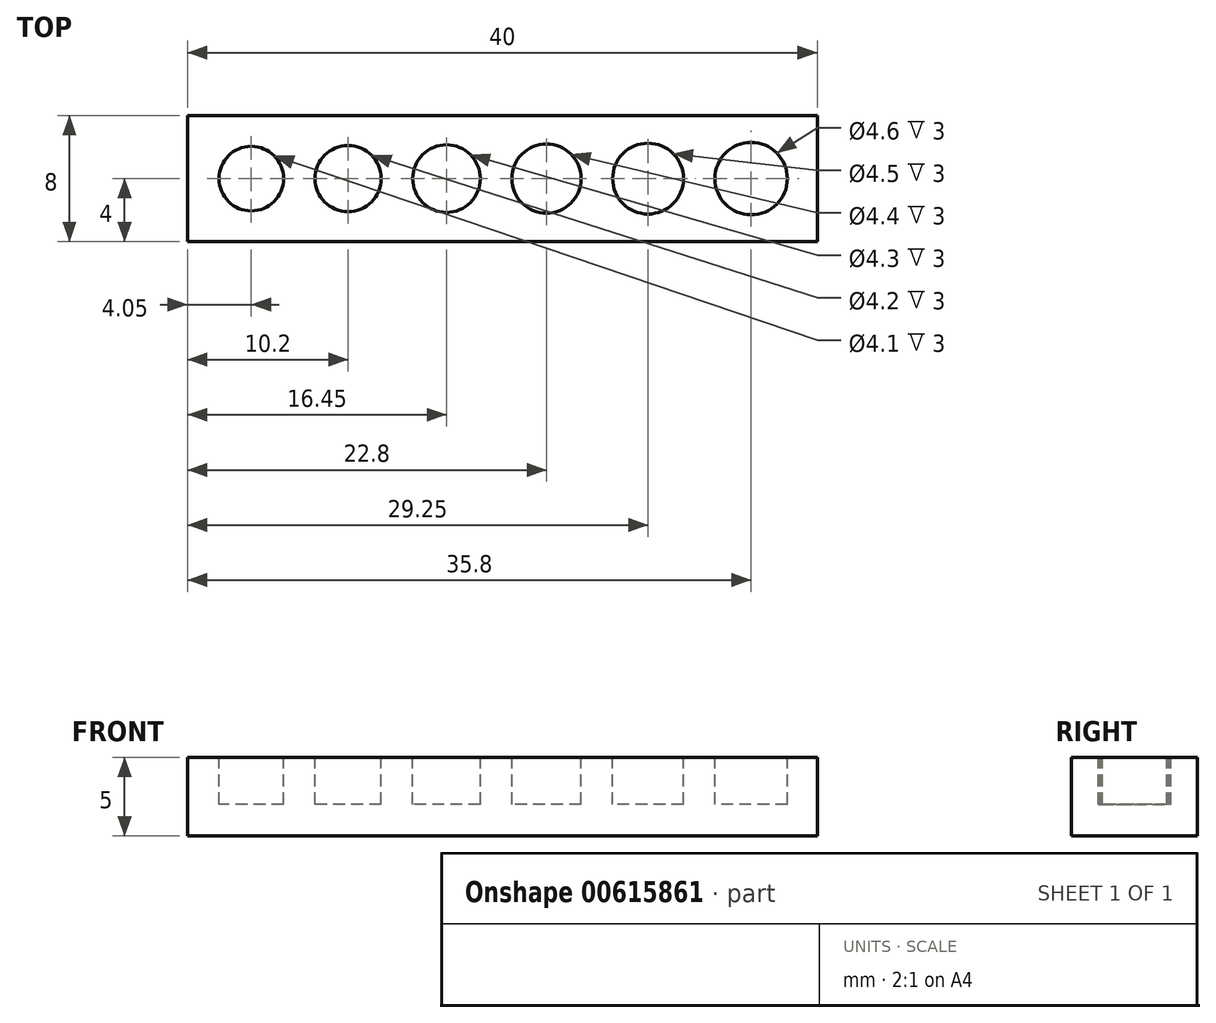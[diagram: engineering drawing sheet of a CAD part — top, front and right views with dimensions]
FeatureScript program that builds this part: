
annotation { "Feature Type Name" : "Feature", "Feature Type Description" : "" }
export const myFeature = defineFeature(function(context is Context, id is Id, definition is map)
    precondition{}
    {
        {
            var Q0;
            Q0=qCreatedBy(makeId("Top.planeOp"),FACE);
            var sketch = newSketch(context, id + "F0", { "sketchPlane" : qUnion([Q0])});
            skLineSegment(sketch, "E0.bottom", {"start": v(0, 0) * mm, "end": v(40, 0) * mm});
            skLineSegment(sketch, "E0.top", {"start": v(0, -8) * mm, "end": v(40, -8) * mm});
            skLineSegment(sketch, "E0.left", {"start": v(0, 0) * mm, "end": v(0, -8) * mm});
            skLineSegment(sketch, "E0.right", {"start": v(40, 0) * mm, "end": v(40, -8) * mm});
            skSolve(sketch);
        }
        {
            var Q0;
            Q0 = qSketchRegion(id + "F0", true);
            extrude(context, id + "F1", {"entities" : qUnion([Q0]), "depth" : 5 * mm, "offsetDistance" : 25 * mm});
        }
        {
            var Q0;
            Q0=makeQuery(id+"F1.opExtrude","CAP_FACE",FACE,{"disambiguationData":[OSD([sQuery(id+"F0.wireOp",EDGE,"E0.bottom"),sQuery(id+"F0.wireOp",EDGE,"E0.top"),sQuery(id+"F0.wireOp",EDGE,"E0.left"),sQuery(id+"F0.wireOp",EDGE,"E0.right")])],"isStart":false});
            var sketch = newSketch(context, id + "F2", { "sketchPlane" : qUnion([Q0])});
            skLineSegment(sketch, "E1", {"start": v(0, -4) * mm, "end": v(40, -4) * mm, "construction": true});
            skCircle(sketch, "E2", {"center": v(4.05, -4) * mm, "radius": 2.05 * mm});
            skCircle(sketch, "E3", {"center": v(10.2, -4) * mm, "radius": 2.1 * mm});
            skCircle(sketch, "E4", {"center": v(16.45, -4) * mm, "radius": 2.15 * mm});
            skCircle(sketch, "E5", {"center": v(22.8, -4) * mm, "radius": 2.2 * mm});
            skCircle(sketch, "E6", {"center": v(29.25, -4) * mm, "radius": 2.25 * mm});
            skCircle(sketch, "E7", {"center": v(35.8, -4) * mm, "radius": 2.3 * mm});
            skSolve(sketch);
        }
        {
            var Q0;
            Q0 = qSketchRegion(id + "F2", true);
            extrude(context, id + "F3", {"entities" : qUnion([Q0]), "operationType" : NewBodyOperationType.REMOVE, "oppositeDirection" : true, "depth" : 3 * mm, "offsetDistance" : 25 * mm});
        }
    });
